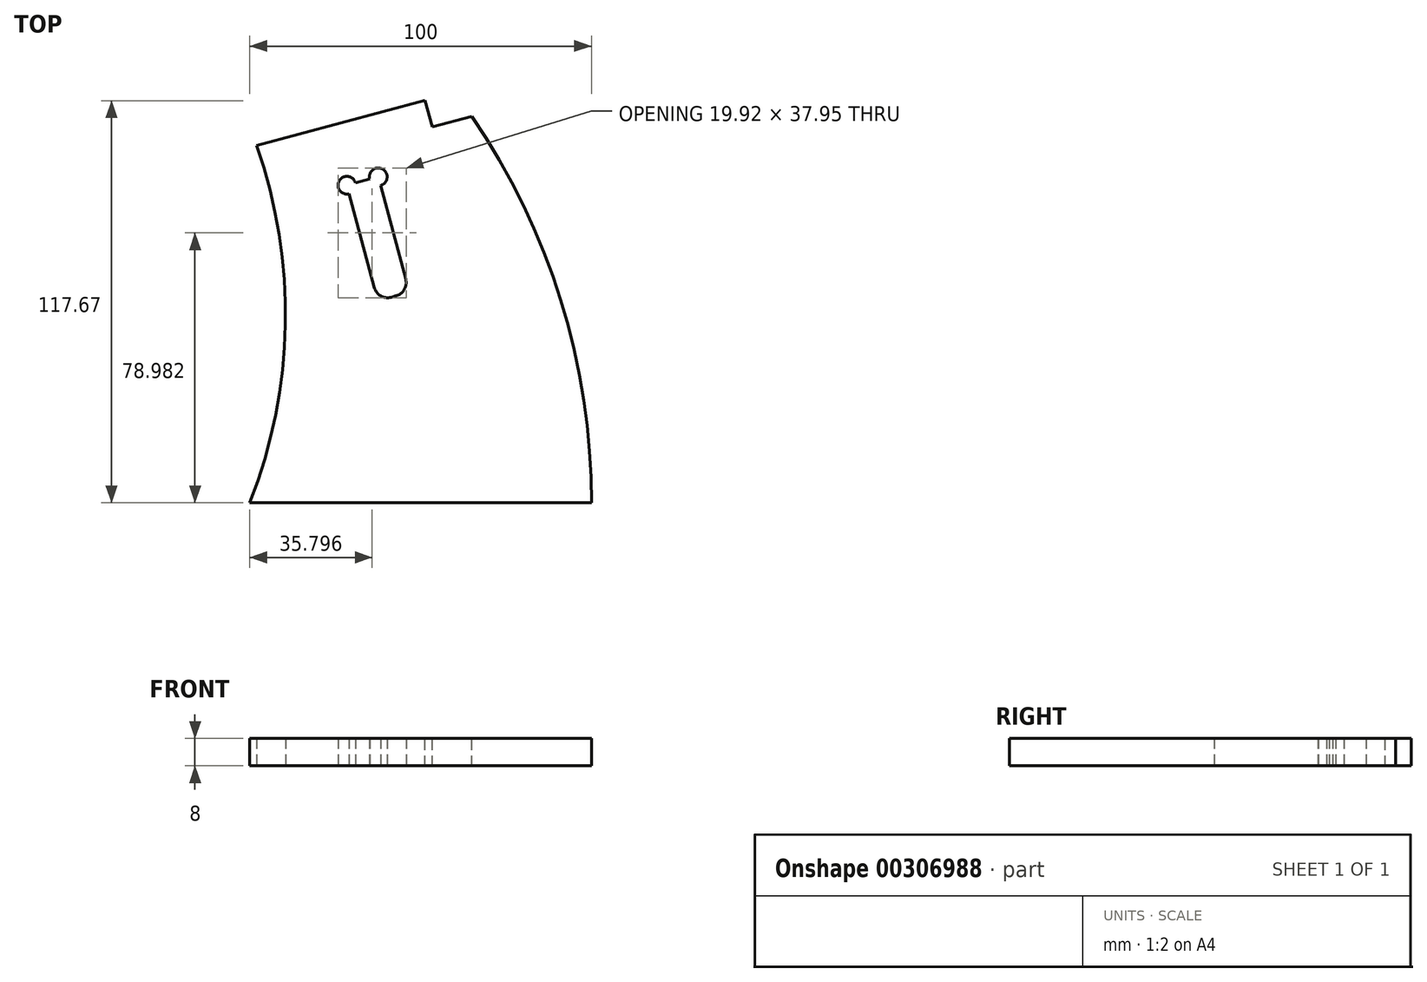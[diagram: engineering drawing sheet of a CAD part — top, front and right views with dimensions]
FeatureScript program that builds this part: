
annotation { "Feature Type Name" : "Feature", "Feature Type Description" : "" }
export const myFeature = defineFeature(function(context is Context, id is Id, definition is map)
    precondition{}
    {
        {
            var Q0;
            Q0=qCreatedBy(makeId("Top.planeOp"),FACE);
            var sketch = newSketch(context, id + "F0", { "sketchPlane" : qUnion([Q0])});
            skLineSegment(sketch, "E0", {"start": v(0, 0) * mm, "end": v(-100, 0) * mm});
            skLineSegment(sketch, "E1", {"start": v(-97.96, 104.47) * mm, "end": v(-40, 120) * mm});
            skArc(sketch, "E2", {"start": v(-100, 0) * mm, "mid": v(-89.59, 52.05) * mm, "end": v(-97.96, 104.47) * mm});
            skArc(sketch, "E3", {"start": v(0, 0) * mm, "mid": v(-10.26, 63.25) * mm, "end": v(-40, 120) * mm});
            skLineSegment(sketch, "E4", {"start": v(0, 0) * mm, "end": v(0, -25.58) * mm, "construction": true});
            skLineSegment(sketch, "E5.top", {"start": v(-58.65, 60.13) * mm, "end": v(-57.2, 60.52) * mm});
            skLineSegment(sketch, "E5.left", {"start": v(-70.8, 90) * mm, "end": v(-63.55, 62.96) * mm});
            skLineSegment(sketch, "E5.right", {"start": v(-61.62, 92.47) * mm, "end": v(-54.37, 65.42) * mm});
            skLineSegment(sketch, "E6.bottom", {"start": v(-71.57, 92.9) * mm, "end": v(-62.4, 95.36) * mm});
            skPoint(sketch, "E7.visualSharp", {"position": v(-62.51, 59.1) * mm});
            skArc(sketch, "E7.filletArc", {"start": v(-63.55, 62.96) * mm, "mid": v(-61.68, 60.53) * mm, "end": v(-58.65, 60.13) * mm});
            skPoint(sketch, "E8.visualSharp", {"position": v(-53.34, 61.56) * mm});
            skArc(sketch, "E8.filletArc", {"start": v(-57.2, 60.52) * mm, "mid": v(-54.77, 62.39) * mm, "end": v(-54.37, 65.42) * mm});
            skLineSegment(sketch, "E9", {"start": v(-57.92, 60.33) * mm, "end": v(-66.98, 94.14) * mm, "construction": true});
            skLineSegment(sketch, "E10", {"start": v(-70.8, 90) * mm, "end": v(-71.57, 92.9) * mm});
            skLineSegment(sketch, "E11", {"start": v(-61.62, 92.47) * mm, "end": v(-62.4, 95.36) * mm});
            skCircle(sketch, "E12", {"center": v(-71.57, 92.9) * mm, "radius": 2.6 * mm});
            skCircle(sketch, "E13", {"center": v(-62.4, 95.36) * mm, "radius": 2.6 * mm});
            skSolve(sketch);
        }
        {
            var Q0;
            Q0=makeQuery(id+"F0.imprint","IMPRINT",FACE,{"disambiguationData":[TD([[makeQuery(id+"F0.imprint","IMPRINT",EDGE,{"derivedFrom":sQuery(id+"F0.wireOp",EDGE,"E0")}),-1.0]])]});
            extrude(context, id + "F1", {"entities" : qUnion([Q0]), "depth" : 8 * mm});
        }
        {
            var Q0;
            Q0=makeQuery(id+"F1.opExtrude","CAP_FACE",FACE,{"disambiguationData":[OSD([sQuery(id+"F0.wireOp",EDGE,"E0"),sQuery(id+"F0.wireOp",EDGE,"E1"),sQuery(id+"F0.wireOp",EDGE,"E2"),sQuery(id+"F0.wireOp",EDGE,"E3"),sQuery(id+"F0.wireOp",EDGE,"E5.top"),sQuery(id+"F0.wireOp",EDGE,"E5.left"),sQuery(id+"F0.wireOp",EDGE,"E5.right"),sQuery(id+"F0.wireOp",EDGE,"E6.bottom"),sQuery(id+"F0.wireOp",EDGE,"E7.filletArc"),sQuery(id+"F0.wireOp",EDGE,"E8.filletArc"),sQuery(id+"F0.wireOp",EDGE,"E10"),sQuery(id+"F0.wireOp",EDGE,"E11"),sQuery(id+"F0.wireOp",EDGE,"E12"),sQuery(id+"F0.wireOp",EDGE,"E13")])],"isStart":false});
            var sketch = newSketch(context, id + "F2", { "sketchPlane" : qUnion([Q0])});
            skLineSegment(sketch, "E14", {"start": v(-46.62, 109.94) * mm, "end": v(-13.9, 118.7) * mm});
            skLineSegment(sketch, "E15", {"start": v(-40, 120) * mm, "end": v(-36.16, 105.66) * mm, "construction": true});
            skLineSegment(sketch, "E16", {"start": v(-46.62, 109.94) * mm, "end": v(-48.7, 117.67) * mm});
            skLineSegment(sketch, "E17.0.0", {"start": v(-40, 120) * mm, "end": v(-97.96, 104.47) * mm});
            skLineSegment(sketch, "E17.0.2", {"start": v(-97.96, 104.47) * mm, "end": v(-40, 120) * mm});
            skSolve(sketch);
        }
        {
            var Q0;
            {var subQ0=sQuery(id+"F2.wireOp",EDGE,"E16");Q0=makeQuery(id+"F2.imprint","IMPRINT",FACE,{"disambiguationData":[TD([[makeQuery(id+"F2.imprint","IMPRINT",EDGE,{"derivedFrom":subQ0}),-1.0]])]});}
            extrude(context, id + "F3", {"entities" : qUnion([Q0]), "operationType" : NewBodyOperationType.REMOVE, "endBound" : BoundingType.THROUGH_ALL, "oppositeDirection" : true, "depth" : 25 * mm});
        }
    });
